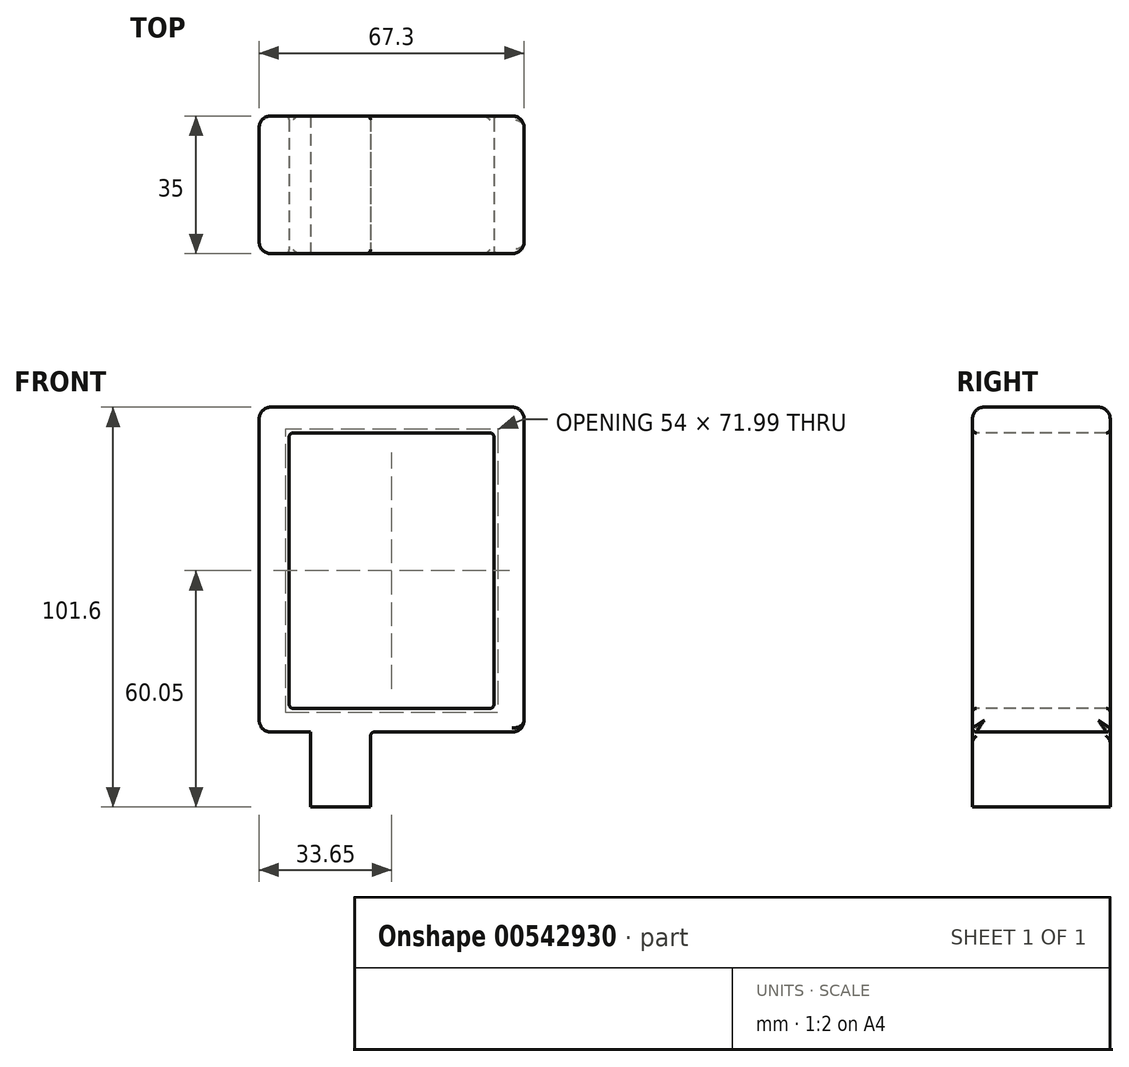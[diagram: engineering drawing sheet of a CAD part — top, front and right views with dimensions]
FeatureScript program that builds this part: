
annotation { "Feature Type Name" : "Feature", "Feature Type Description" : "" }
export const myFeature = defineFeature(function(context is Context, id is Id, definition is map)
    precondition{}
    {
        {
            var Q0;
            Q0=qCreatedBy(makeId("Front.planeOp"),FACE);
            var sketch = newSketch(context, id + "F0", { "sketchPlane" : qUnion([Q0])});
            skLineSegment(sketch, "E0", {"start": v(-20.65, 19.05) * mm, "end": v(-33.65, 19.05) * mm});
            skLineSegment(sketch, "E1", {"start": v(-33.65, 19.05) * mm, "end": v(-33.65, 101.6) * mm});
            skLineSegment(sketch, "E2", {"start": v(-33.65, 101.6) * mm, "end": v(0, 101.6) * mm});
            skLineSegment(sketch, "E3", {"start": v(0, 101.6) * mm, "end": v(0, 0) * mm});
            skLineSegment(sketch, "E4.MirrorCS", {"start": v(33.65, 101.6) * mm, "end": v(0, 101.6) * mm});
            skLineSegment(sketch, "E5.MirrorCS", {"start": v(33.65, 19.05) * mm, "end": v(33.65, 101.6) * mm});
            skLineSegment(sketch, "E6.MirrorCS", {"start": v(7.65, 19.05) * mm, "end": v(33.65, 19.05) * mm});
            skLineSegment(sketch, "E7", {"start": v(-5.35, 19.05) * mm, "end": v(7.65, 19.05) * mm});
            skPoint(sketch, "E8.MirrorCS.start.orphan", {"position": v(0, 0) * mm});
            skLineSegment(sketch, "E9", {"start": v(-20.65, 19.05) * mm, "end": v(-20.65, 0) * mm});
            skLineSegment(sketch, "E10", {"start": v(-20.65, 0) * mm, "end": v(-5.35, 0) * mm});
            skLineSegment(sketch, "E11", {"start": v(-5.35, 0) * mm, "end": v(-5.35, 19.05) * mm});
            skSolve(sketch);
        }
        {
            var Q0;
            Q0=qSketchRegion(id+"F0",true);
            extrude(context, id + "F1", {"entities" : qUnion([Q0]), "oppositeDirection" : true, "depth" : 35 * mm, "offsetDistance" : 25 * mm});
        }
        {
            var Q0;
            Q0=makeQuery(id+"F1.opExtrude","CAP_FACE",FACE,{"disambiguationData":[OSD([sQuery(id+"F0.wireOp",EDGE,"sP7V6Udn-upoT-n5cL-rasM-UTym57IdEnWT"),sQuery(id+"F0.wireOp",EDGE,"SEUvbFxk-v5BC-gieZ-ReZB-7vY9yVAJOFBW"),sQuery(id+"F0.wireOp",EDGE,"E0"),sQuery(id+"F0.wireOp",EDGE,"E1"),sQuery(id+"F0.wireOp",EDGE,"E2"),sQuery(id+"F0.wireOp",EDGE,"E4.MirrorCS"),sQuery(id+"F0.wireOp",EDGE,"E5.MirrorCS"),sQuery(id+"F0.wireOp",EDGE,"E6.MirrorCS"),sQuery(id+"F0.wireOp",EDGE,"fc3f467f-0655-4689-9aec-43b8ef272ecf0.MirrorCS"),sQuery(id+"F0.wireOp",EDGE,"E8.MirrorCS")])],"isStart":true});
            var sketch = newSketch(context, id + "F2", { "sketchPlane" : qUnion([Q0])});
            skLineSegment(sketch, "E12", {"start": v(0, 25.05) * mm, "end": v(-26, 25.05) * mm});
            skLineSegment(sketch, "E13", {"start": v(-26, 25.05) * mm, "end": v(-26, 95.05) * mm});
            skLineSegment(sketch, "E14", {"start": v(-26, 95.05) * mm, "end": v(0, 95.05) * mm});
            skLineSegment(sketch, "E15.MirrorCS", {"start": v(26, 95.05) * mm, "end": v(0, 95.05) * mm});
            skLineSegment(sketch, "E16.MirrorCS", {"start": v(26, 25.05) * mm, "end": v(26, 95.05) * mm});
            skLineSegment(sketch, "E17.MirrorCS", {"start": v(0, 25.05) * mm, "end": v(26, 25.05) * mm});
            skSolve(sketch);
        }
        {
            var Q0;
            Q0=qSketchRegion(id+"F2",true);
            extrude(context, id + "F3", {"entities" : qUnion([Q0]), "operationType" : NewBodyOperationType.REMOVE, "endBound" : BoundingType.THROUGH_ALL, "oppositeDirection" : true, "depth" : 25 * mm, "offsetDistance" : 25 * mm});
        }
        {
            var Q0;
            Q0=makeQuery(id+"F1.opExtrude","SWEPT_FACE",FACE,{"disambiguationData":[OSD([sQuery(id+"F0.wireOp",EDGE,"E2"),sQuery(id+"F0.wireOp",EDGE,"E4.MirrorCS")])]});
            var Q1;
            Q1=makeQuery(id+"F1.opExtrude","SWEPT_FACE",FACE,{"disambiguationData":[OSD([sQuery(id+"F0.wireOp",EDGE,"E5.MirrorCS")])]});
            var Q2;
            Q2=makeQuery(id+"F1.opExtrude","SWEPT_FACE",FACE,{"disambiguationData":[OSD([sQuery(id+"F0.wireOp",EDGE,"E1")])]});
            fillet(context, id + "F4", {"entities" : qUnion([Q0, Q1, Q2]), "radius" : 3 * mm, "tangentPropagation" : true, "allowEdgeOverflow" : false});
        }
        {
            var Q0;
            Q0=makeQuery(id+"F1.opExtrude","SWEPT_FACE",FACE,{"disambiguationData":[OSD([sQuery(id+"F0.wireOp",EDGE,"SEUvbFxk-v5BC-gieZ-ReZB-7vY9yVAJOFBW")])]});
            var Q1;
            Q1=makeQuery(id+"F1.opExtrude","SWEPT_FACE",FACE,{"disambiguationData":[OSD([sQuery(id+"F0.wireOp",EDGE,"E6.MirrorCS")])]});
            var Q2;
            Q2=makeQuery(id+"F1.opExtrude","SWEPT_FACE",FACE,{"disambiguationData":[OSD([sQuery(id+"F0.wireOp",EDGE,"sP7V6Udn-upoT-n5cL-rasM-UTym57IdEnWT"),sQuery(id+"F0.wireOp",EDGE,"E8.MirrorCS")])]});
            var Q3;
            Q3=makeQuery(id+"F3.boolean.opBoolean","COPY",FACE,{"derivedFrom":makeQuery(id+"F3.opExtrude","SWEPT_FACE",FACE,{"disambiguationData":[OSD([sQuery(id+"F2.wireOp",EDGE,"E13")])]})});
            var Q4;
            Q4=makeQuery(id+"F3.boolean.opBoolean","COPY",FACE,{"derivedFrom":makeQuery(id+"F3.opExtrude","SWEPT_FACE",FACE,{"disambiguationData":[OSD([sQuery(id+"F2.wireOp",EDGE,"E16.MirrorCS")])]})});
            fillet(context, id + "F5", {"entities" : qUnion([Q0, Q1, Q2, Q3, Q4]), "radius" : 1 * mm, "tangentPropagation" : true, "allowEdgeOverflow" : false});
        }
    });
